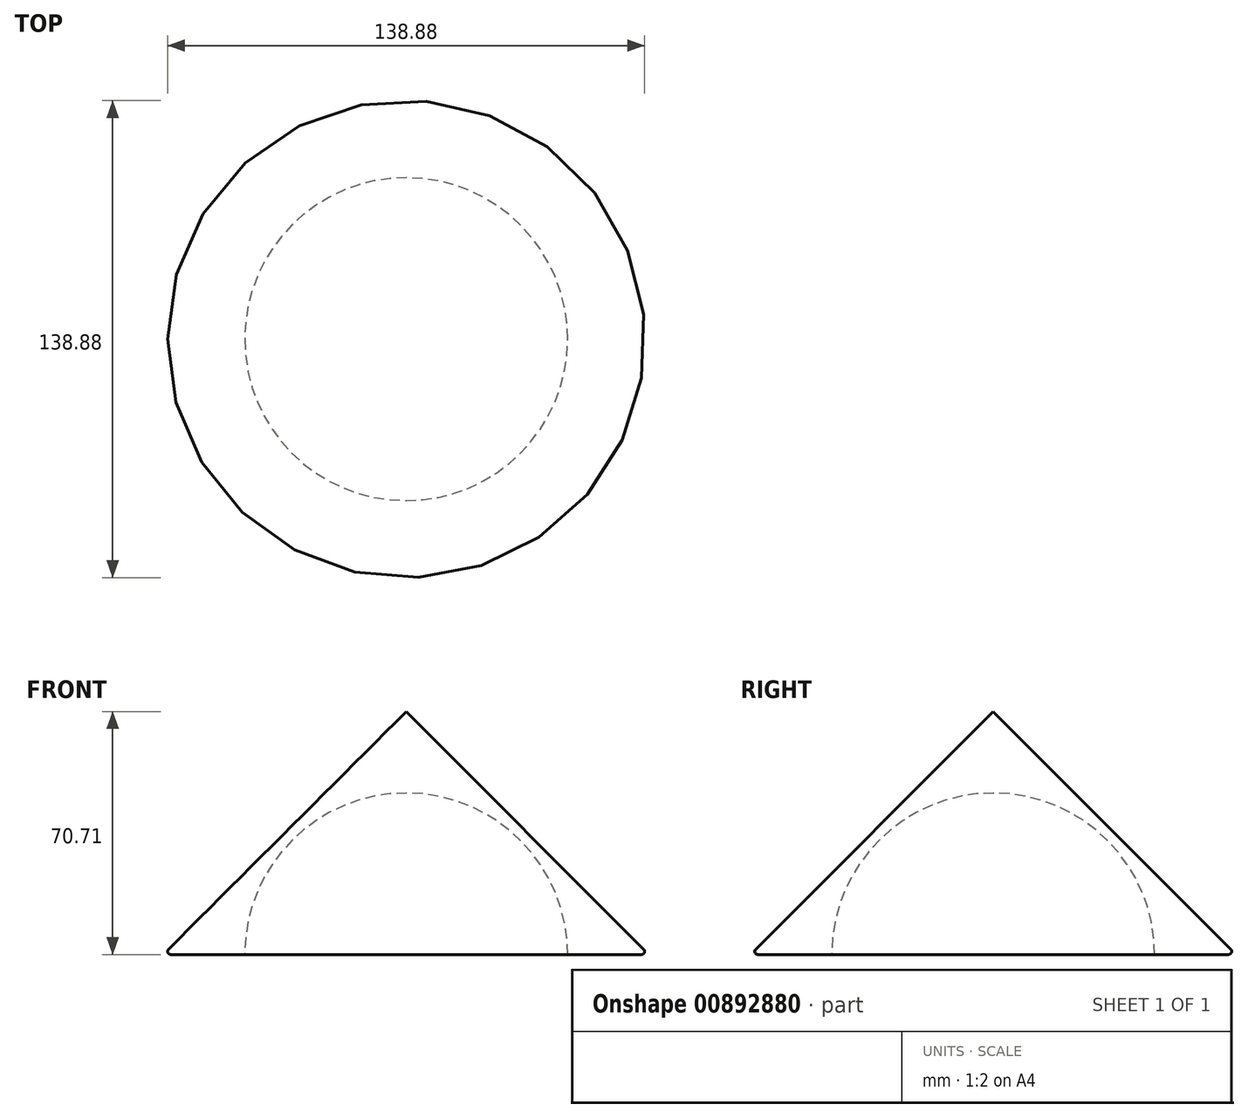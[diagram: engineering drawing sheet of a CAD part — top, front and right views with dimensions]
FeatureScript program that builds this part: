
annotation { "Feature Type Name" : "Feature", "Feature Type Description" : "" }
export const myFeature = defineFeature(function(context is Context, id is Id, definition is map)
    precondition{}
    {
        {
            var Q0;
            Q0=qCreatedBy(makeId("Front.planeOp"),FACE);
            var sketch = newSketch(context, id + "F0", { "sketchPlane" : qUnion([Q0])});
            skLineSegment(sketch, "E0", {"start": v(0, 0) * mm, "end": v(-70.71, 0) * mm});
            skLineSegment(sketch, "E1", {"start": v(0, 0) * mm, "end": v(0, 70.71) * mm});
            skLineSegment(sketch, "E2", {"start": v(-70.71, 0) * mm, "end": v(0, 70.71) * mm});
            skSolve(sketch);
        }
        {
            var Q0;
            Q0 = qSketchRegion(id + "F0", true);
            var Q1;
            Q1=sQuery(id+"F0.wireOp",EDGE,"E1");
            revolve(context, id + "F1", {"surfaceOperationType" : NewSurfaceOperationType.NEW, "entities" : qUnion([Q0]), "axis" : qUnion([Q1]), "revolveType" : RevolveType.FULL});
        }
        {
            var Q0;
            Q0=qCreatedBy(makeId("Front.planeOp"),FACE);
            var sketch = newSketch(context, id + "F2", { "sketchPlane" : qUnion([Q0])});
            skCircle(sketch, "E3", {"center": v(0, 0) * mm, "radius": 47 * mm});
            skLineSegment(sketch, "E4", {"start": v(-47, 0) * mm, "end": v(47, 0) * mm});
            skSolve(sketch);
        }
        {
            var Q0;
            {var subQ0=sQuery(id+"F2.wireOp",EDGE,"E4");Q0=makeQuery(id+"F2.imprint","IMPRINT",FACE,{"disambiguationData":[TD([[makeQuery(id+"F2.imprint","IMPRINT",EDGE,{"derivedFrom":subQ0}),-1.0]])]});}
            var Q1;
            Q1=sQuery(id+"F2.wireOp",EDGE,"E4");
            revolve(context, id + "F3", {"operationType" : NewBodyOperationType.REMOVE, "surfaceOperationType" : NewSurfaceOperationType.NEW, "entities" : qUnion([Q0]), "axis" : qUnion([Q1]), "revolveType" : RevolveType.FULL, "oppositeDirection" : true});
        }
        {
            var Q0;
            Q0=makeQuery(id+"F1.opRevolve","SWEPT_EDGE",EDGE,{"disambiguationData":[OSD([sQuery(id+"F0.wireOp",EDGE,"E0"),sQuery(id+"F0.wireOp",EDGE,"E2")])]});
            fillet(context, id + "F4", {"entities" : qUnion([Q0]), "radius" : 0.9 * mm, "tangentPropagation" : true, "allowEdgeOverflow" : false});
        }
    });
